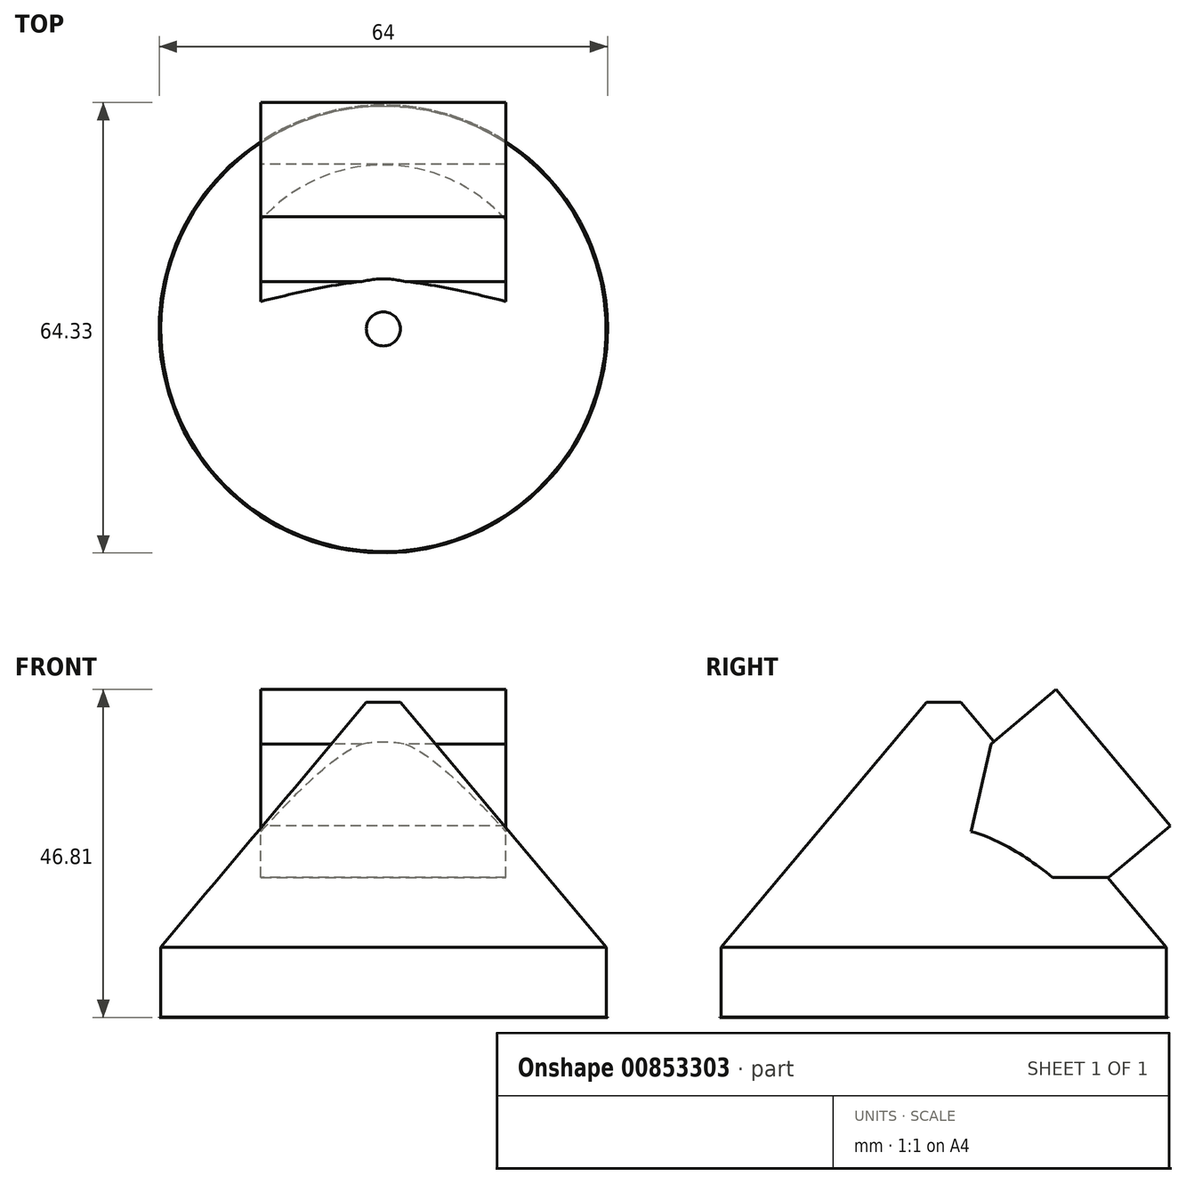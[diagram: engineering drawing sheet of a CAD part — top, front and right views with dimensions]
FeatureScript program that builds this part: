
annotation { "Feature Type Name" : "Feature", "Feature Type Description" : "" }
export const myFeature = defineFeature(function(context is Context, id is Id, definition is map)
    precondition{}
    {
        {
            var Q0;
            Q0=qCreatedBy(makeId("Top.planeOp"),FACE);
            var sketch = newSketch(context, id + "F0", { "sketchPlane" : qUnion([Q0])});
            skCircle(sketch, "E0", {"center": v(0, 0) * mm, "radius": 32 * mm});
            skSolve(sketch);
        }
        {
            var Q0;
            Q0=makeQuery(id+"F0.imprint","IMPRINT",FACE,{"disambiguationData":[TD([[makeQuery(id+"F0.imprint","IMPRINT",EDGE,{"derivedFrom":sQuery(id+"F0.wireOp",EDGE,"E0")}),1.0]])]});
            extrude(context, id + "F1", {"entities" : qUnion([Q0]), "depth" : 10 * mm, "offsetDistance" : 25 * mm});
        }
        {
            var Q0;
            Q0=makeQuery(id+"F1.opExtrude","CAP_FACE",FACE,{"disambiguationData":[OSD([sQuery(id+"F0.wireOp",EDGE,"E0")])],"isStart":false});
            extrude(context, id + "F2", {"entities" : qUnion([Q0]), "operationType" : NewBodyOperationType.ADD, "depth" : 35 * mm, "offsetDistance" : 25 * mm});
        }
        {
            var Q0;
            Q0=qCreatedBy(makeId("Right.planeOp"),FACE);
            var sketch = newSketch(context, id + "F3", { "sketchPlane" : qUnion([Q0])});
            skLineSegment(sketch, "E1", {"start": v(0.3, 47.54) * mm, "end": v(31.8, 10) * mm});
            skLineSegment(sketch, "E2", {"start": v(31.8, 10) * mm, "end": v(31.8, 0) * mm});
            skLineSegment(sketch, "E3", {"start": v(0, 50.78) * mm, "end": v(0, -2.28) * mm, "construction": true});
            skLineSegment(sketch, "E4", {"start": v(31.8, 10) * mm, "end": v(3.29, 10) * mm});
            skLineSegment(sketch, "E5", {"start": v(0.3, 47.54) * mm, "end": v(35.55, 47.54) * mm});
            skLineSegment(sketch, "E6", {"start": v(31.8, 0) * mm, "end": v(39.02, 1.34) * mm});
            skLineSegment(sketch, "E7", {"start": v(39.02, 1.34) * mm, "end": v(40.08, 13.93) * mm});
            skLineSegment(sketch, "E8", {"start": v(40.08, 13.93) * mm, "end": v(35.55, 47.54) * mm});
            skSolve(sketch);
        }
        {
            var Q0;
            Q0=makeQuery(id+"F3.imprint","IMPRINT",FACE,{"disambiguationData":[TD([[makeQuery(id+"F3.imprint","IMPRINT",EDGE,{"derivedFrom":sQuery(id+"F3.wireOp",EDGE,"E1")}),1.0]])]});
            var Q1;
            Q1=sQuery(id+"F3.wireOp",EDGE,"E3");
            revolve(context, id + "F4", {"operationType" : NewBodyOperationType.REMOVE, "surfaceOperationType" : NewSurfaceOperationType.NEW, "entities" : qUnion([Q0]), "axis" : qUnion([Q1]), "revolveType" : RevolveType.FULL, "oppositeDirection" : true});
        }
        {
            var Q0;
            Q0=qCreatedBy(makeId("Right.planeOp"),FACE);
            var sketch = newSketch(context, id + "F5", { "sketchPlane" : qUnion([Q0])});
            skLineSegment(sketch, "E9", {"start": v(16, 46.81) * mm, "end": v(38.5, 20) * mm});
            skLineSegment(sketch, "E10", {"start": v(38.5, 20) * mm, "end": v(2.46, 20) * mm});
            skLineSegment(sketch, "E11", {"start": v(16, 46.81) * mm, "end": v(6.75, 39.04) * mm});
            skLineSegment(sketch, "E12", {"start": v(6.75, 39.04) * mm, "end": v(2.46, 20) * mm});
            skLineSegment(sketch, "E13", {"start": v(23.55, 20) * mm, "end": v(32.33, 27.36) * mm});
            skSolve(sketch);
        }
        {
            var Q0;
            {var subQ0=sQuery(id+"F5.wireOp",EDGE,"E11");Q0=makeQuery(id+"F5.imprint","IMPRINT",FACE,{"disambiguationData":[TD([[makeQuery(id+"F5.imprint","IMPRINT",EDGE,{"derivedFrom":subQ0}),1.0]])]});}
            extrude(context, id + "F6", {"entities" : qUnion([Q0]), "operationType" : NewBodyOperationType.ADD, "endBound" : BoundingType.SYMMETRIC, "depth" : 35 * mm, "offsetDistance" : 25 * mm});
        }
    });
